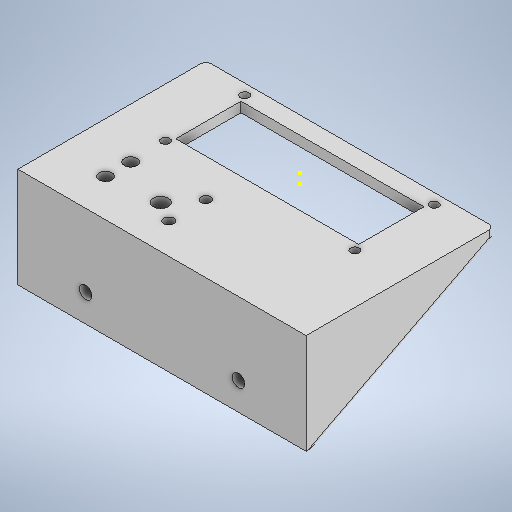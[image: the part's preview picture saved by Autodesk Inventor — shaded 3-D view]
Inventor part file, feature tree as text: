
AUTODESK INVENTOR PART (.ipt)
format: ipt  version: 2025.2 (Build 292293000, 293)  size: 453,632 bytes
history: native  units: mm
features: sketch x17, extrude x12, fillet x5, hole x3, mirror x2, other x1
ambient origin geometry x8: Origin, YZ Plane, XZ Plane, XY Plane, X Axis, Y Axis, Z Axis, Center Point
bodies: Body1 (feature_tree)
feature tree (40):
  other  "Bryła1"
  extrude  "Wyciągnięcie proste1"  Depth=85.0mm
  hole  "Otwór1"  [1 undecoded]
  extrude  "Wyciągnięcie proste2"  Depth=4.0mm TaperAngle=0.0deg
  extrude  "Wyciągnięcie proste3"  Depth=75.6mm
  extrude  "Wyciągnięcie proste4"  Depth=31.6mm
  sketch  "Szkic6"
  extrude  "Wyciągnięcie proste5"  Depth=73.0mm
  mirror  "Odbij1"
  extrude  "Wyciągnięcie proste6"  Depth=26.0mm
  extrude  "Wyciągnięcie proste7"  TaperAngle=0.0deg  [1 undecoded]
  extrude  "Wyciągnięcie proste8"  Depth=85.0mm
  mirror  "Odbij2"
  fillet  "Zaokrąglenie1"  Radius=30.0mm
  fillet  "Zaokrąglenie2"  Radius=4.0mm
  fillet  "Zaokrąglenie3"  Radius=100.0mm
  fillet  "Zaokrąglenie4"  Radius=40.0mm
  extrude  "Wyciągnięcie proste9"  Depth=5.0mm TaperAngle=0.0deg
  fillet  "Zaokrąglenie5"  Radius=15.0mm
  extrude  "Wyciągnięcie proste10"  Depth=75.0mm
  extrude  "Wyciągnięcie proste11"  Depth=4.0mm TaperAngle=0.0deg
  hole  "Otwór2"  [1 undecoded]
  hole  "Otwór3"  [1 undecoded]
  extrude  "Wyciągnięcie proste12"  Depth=10.0mm
  sketch  "Szkic19"
  sketch  "Szkic1"
  sketch  "Szkic2"
  sketch  "Szkic3"
  sketch  "Szkic4"
  sketch  "Szkic5"
  sketch  "Szkic7"
  sketch  "Szkic8"
  sketch  "Szkic9"
  sketch  "Szkic10"
  sketch  "Szkic12"
  sketch  "Szkic13"
  sketch  "Szkic15"
  sketch  "Szkic16"
  sketch  "Szkic17"
  sketch  "Szkic18"
note: 4 required parameter values undecoded (feature->parameter linkage not recoverable at this tier; creation-order binding heuristic only, values carry confidence <= 0.55)
